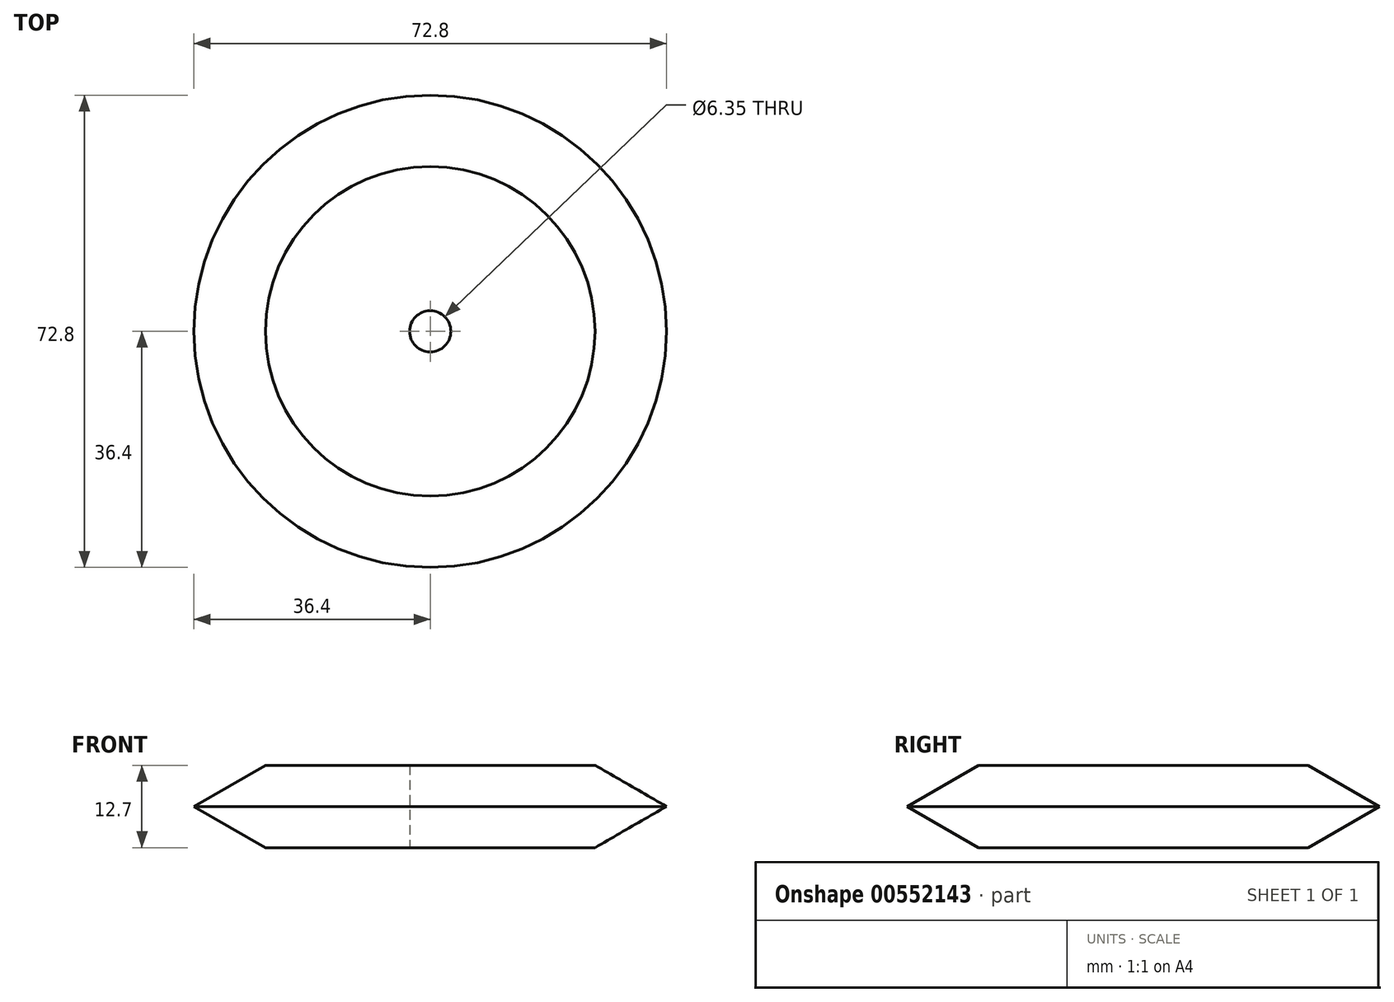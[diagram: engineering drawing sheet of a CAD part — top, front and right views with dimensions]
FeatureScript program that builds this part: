
annotation { "Feature Type Name" : "Feature", "Feature Type Description" : "" }
export const myFeature = defineFeature(function(context is Context, id is Id, definition is map)
    precondition{}
    {
        {
            var Q0;
            Q0=qCreatedBy(makeId("Front.planeOp"),FACE);
            var sketch = newSketch(context, id + "F0", { "sketchPlane" : qUnion([Q0])});
            skLineSegment(sketch, "E0.bottom", {"start": v(-25.4, 12.7) * mm, "end": v(0, 12.7) * mm});
            skLineSegment(sketch, "E0.top", {"start": v(-25.4, 0) * mm, "end": v(0, 0) * mm});
            skLineSegment(sketch, "E0.left", {"start": v(-25.4, 12.7) * mm, "end": v(-25.4, 0) * mm});
            skLineSegment(sketch, "E0.right", {"start": v(0, 12.7) * mm, "end": v(0, 0) * mm});
            skLineSegment(sketch, "E1", {"start": v(-25.4, 12.7) * mm, "end": v(-36.4, 6.35) * mm});
            skPoint(sketch, "E1.endSnap0", {"position": v(-25.4, 6.35) * mm});
            skLineSegment(sketch, "E2", {"start": v(-36.4, 6.35) * mm, "end": v(-25.4, 0) * mm});
            skSolve(sketch);
        }
        {
            var Q0;
            Q0=makeQuery(id+"F0.imprint","IMPRINT",FACE,{"disambiguationData":[TD([[makeQuery(id+"F0.imprint","IMPRINT",EDGE,{"derivedFrom":sQuery(id+"F0.wireOp",EDGE,"E0.bottom")}),-1.0]])]});
            var Q1;
            Q1=makeQuery(id+"F0.imprint","IMPRINT",FACE,{"disambiguationData":[TD([[makeQuery(id+"F0.imprint","IMPRINT",EDGE,{"derivedFrom":sQuery(id+"F0.wireOp",EDGE,"E0.left")}),-1.0]])]});
            var Q2;
            Q2=sQuery(id+"F0.wireOp",EDGE,"E0.right");
            revolve(context, id + "F1", {"entities" : qUnion([Q0, Q1]), "axis" : qUnion([Q2]), "revolveType" : RevolveType.FULL});
        }
        {
            var Q0;
            Q0=makeQuery(id+"F1.opRevolve","SWEPT_FACE",FACE,{"disambiguationData":[OSD([sQuery(id+"F0.wireOp",EDGE,"E0.top")])]});
            var sketch = newSketch(context, id + "F2", { "sketchPlane" : qUnion([Q0])});
            skCircle(sketch, "E3", {"center": v(0, 0) * mm, "radius": 3.18 * mm});
            skSolve(sketch);
        }
        {
            var Q0;
            Q0 = qSketchRegion(id + "F2", true);
            extrude(context, id + "F3", {"entities" : qUnion([Q0]), "operationType" : NewBodyOperationType.REMOVE, "oppositeDirection" : true, "depth" : 12.7 * mm, "offsetDistance" : 25.4 * mm});
        }
    });
